annotation { "Feature Type Name" : "Feature", "Feature Type Description" : "" }
export const myFeature = defineFeature(function(context is Context, id is Id, definition is map)
    precondition{}
    {
        {
            var Q0;
            Q0=qCreatedBy(makeId("Top.planeOp"),FACE);
            var sketch = newSketch(context, id + "F0", { "sketchPlane" : qUnion([Q0])});
            skPoint(sketch, "E0.middle", {"position": v(0, 0) * mm});
            skLineSegment(sketch, "E1.bottom", {"start": v(-10, 19) * mm, "end": v(10, 19) * mm});
            skLineSegment(sketch, "E1.top", {"start": v(-10, -19) * mm, "end": v(10, -19) * mm});
            skLineSegment(sketch, "E1.left", {"start": v(-10, 19) * mm, "end": v(-10, -19) * mm});
            skLineSegment(sketch, "E1.right", {"start": v(10, 19) * mm, "end": v(10, -19) * mm});
            skArc(sketch, "E2.filletArc", {"start": v(-17, 30) * mm, "mid": v(-22.66, 27.66) * mm, "end": v(-25, 22) * mm});
            skPoint(sketch, "E3.visualSharp", {"position": v(25, 30) * mm});
            skArc(sketch, "E3.filletArc", {"start": v(25, 22) * mm, "mid": v(22.66, 27.66) * mm, "end": v(17, 30) * mm});
            skArc(sketch, "E4.filletArc", {"start": v(17, -30) * mm, "mid": v(22.66, -27.66) * mm, "end": v(25, -22) * mm});
            skArc(sketch, "E5.filletArc", {"start": v(-25, -22) * mm, "mid": v(-22.66, -27.66) * mm, "end": v(-17, -30) * mm});
            skCircle(sketch, "E6", {"center": v(-19, 24) * mm, "radius": 1.25 * mm});
            skCircle(sketch, "E7.MirrorC", {"center": v(19, 24) * mm, "radius": 1.25 * mm});
            skCircle(sketch, "E8.MirrorC", {"center": v(19, -24) * mm, "radius": 1.25 * mm});
            skCircle(sketch, "E9.MirrorC", {"center": v(-19, -24) * mm, "radius": 1.25 * mm});
            skLineSegment(sketch, "E10.bottom", {"start": v(-14.5, 18) * mm, "end": v(-12.5, 18) * mm});
            skLineSegment(sketch, "E10.top", {"start": v(-12.5, 6) * mm, "end": v(-12.5, 6) * mm});
            skLineSegment(sketch, "E10.left", {"start": v(-14.5, 18) * mm, "end": v(-14.5, 7.49) * mm});
            skLineSegment(sketch, "E10.right", {"start": v(-12.5, 18) * mm, "end": v(-12.5, 6) * mm});
            skLineSegment(sketch, "E11", {"start": v(-10, 25.5) * mm, "end": v(10, 25.5) * mm});
            skLineSegment(sketch, "E12", {"start": v(-17, 30) * mm, "end": v(-14, 30) * mm});
            skLineSegment(sketch, "E13", {"start": v(-10, 25.5) * mm, "end": v(-14, 30) * mm});
            skLineSegment(sketch, "E14", {"start": v(10, 25.5) * mm, "end": v(14, 30) * mm});
            skLineSegment(sketch, "E15", {"start": v(-17, -30) * mm, "end": v(-14, -30) * mm});
            skLineSegment(sketch, "E16", {"start": v(14, 30) * mm, "end": v(17, 30) * mm});
            skLineSegment(sketch, "E17", {"start": v(-14, -30) * mm, "end": v(-7.22, -22) * mm});
            skLineSegment(sketch, "E18", {"start": v(17, -30) * mm, "end": v(14, -30) * mm});
            skLineSegment(sketch, "E19", {"start": v(14, -30) * mm, "end": v(7.22, -22) * mm});
            skLineSegment(sketch, "E20", {"start": v(-25, -22) * mm, "end": v(-25, -19) * mm});
            skLineSegment(sketch, "E21", {"start": v(-25, 22) * mm, "end": v(-25, 19) * mm});
            skLineSegment(sketch, "E22", {"start": v(25, 22) * mm, "end": v(25, 19) * mm});
            skLineSegment(sketch, "E23", {"start": v(25, -22) * mm, "end": v(25, -19) * mm});
            skLineSegment(sketch, "E24", {"start": v(-20.5, -15) * mm, "end": v(-20.5, 15) * mm});
            skLineSegment(sketch, "E25", {"start": v(-25, -19) * mm, "end": v(-20.5, -15) * mm});
            skLineSegment(sketch, "E26", {"start": v(-20.5, 15) * mm, "end": v(-25, 19) * mm});
            skLineSegment(sketch, "E27", {"start": v(20.5, -15) * mm, "end": v(20.5, 15) * mm});
            skLineSegment(sketch, "E28", {"start": v(20.5, 15) * mm, "end": v(25, 19) * mm});
            skLineSegment(sketch, "E29", {"start": v(20.5, -15) * mm, "end": v(25, -19) * mm});
            skLineSegment(sketch, "E30", {"start": v(-9.92, -25.2) * mm, "end": v(-20.5, -15) * mm, "construction": true});
            skLineSegment(sketch, "E31", {"start": v(9.92, -25.2) * mm, "end": v(20.5, -15) * mm, "construction": true});
            skLineSegment(sketch, "E32", {"start": v(-20.5, 15) * mm, "end": v(-10, 25.5) * mm, "construction": true});
            skLineSegment(sketch, "E33", {"start": v(20.5, 15) * mm, "end": v(10, 25.5) * mm, "construction": true});
            skPoint(sketch, "E34.endSnap0", {"position": v(-20.5, 0) * mm});
            skArc(sketch, "E35.trimOffspring", {"start": v(-18.5, -6) * mm, "mid": v(-12.52, 0) * mm, "end": v(-18.5, 6) * mm});
            skArc(sketch, "E36.0", {"start": v(-18.5, -8.5) * mm, "mid": v(-10.02, 0) * mm, "end": v(-18.5, 8.5) * mm});
            skLineSegment(sketch, "E37", {"start": v(-18.5, 8.5) * mm, "end": v(-20.5, 8.5) * mm});
            skLineSegment(sketch, "E38", {"start": v(-18.5, 6) * mm, "end": v(-20.5, 6) * mm});
            skLineSegment(sketch, "E39", {"start": v(-18.5, -8.5) * mm, "end": v(-20.5, -8.5) * mm});
            skLineSegment(sketch, "E40", {"start": v(-18.5, -6) * mm, "end": v(-20.5, -6) * mm});
            skArc(sketch, "E41.MirrorCS", {"start": v(18.5, -8.5) * mm, "mid": v(10.02, 0) * mm, "end": v(18.5, 8.5) * mm});
            skArc(sketch, "E42.MirrorCS", {"start": v(18.5, -6) * mm, "mid": v(12.52, 0) * mm, "end": v(18.5, 6) * mm});
            skLineSegment(sketch, "E43.MirrorCS", {"start": v(18.5, -8.5) * mm, "end": v(20.5, -8.5) * mm});
            skLineSegment(sketch, "E44.MirrorCS", {"start": v(18.5, -6) * mm, "end": v(20.5, -6) * mm});
            skLineSegment(sketch, "E45.MirrorCS", {"start": v(18.5, 6) * mm, "end": v(20.5, 6) * mm});
            skLineSegment(sketch, "E46.MirrorCS", {"start": v(18.5, 8.5) * mm, "end": v(20.5, 8.5) * mm});
            skPoint(sketch, "E47.orphan", {"position": v(-14.5, 6) * mm});
            skLineSegment(sketch, "E48.MirrorCS", {"start": v(12.5, 18) * mm, "end": v(12.5, 6) * mm});
            skLineSegment(sketch, "E49.MirrorCS", {"start": v(14.5, 18) * mm, "end": v(14.5, 7.49) * mm});
            skLineSegment(sketch, "E50.MirrorCS", {"start": v(14.5, 18) * mm, "end": v(12.5, 18) * mm});
            skLineSegment(sketch, "E51.MirrorCS", {"start": v(14.5, -18) * mm, "end": v(14.5, -7.49) * mm});
            skLineSegment(sketch, "E52.MirrorCS", {"start": v(12.5, -18) * mm, "end": v(12.5, -6) * mm});
            skLineSegment(sketch, "E53.MirrorCS", {"start": v(14.5, -18) * mm, "end": v(12.5, -18) * mm});
            skLineSegment(sketch, "E54.MirrorCS", {"start": v(-12.5, -18) * mm, "end": v(-12.5, -6) * mm});
            skLineSegment(sketch, "E55.MirrorCS", {"start": v(-14.5, -18) * mm, "end": v(-14.5, -7.49) * mm});
            skLineSegment(sketch, "E56.MirrorCS", {"start": v(-14.5, -18) * mm, "end": v(-12.5, -18) * mm});
            skLineSegment(sketch, "E57.0", {"start": v(-7.22, -22) * mm, "end": v(7.22, -22) * mm});
            skLineSegment(sketch, "E58", {"start": v(0, 19) * mm, "end": v(0, 25.5) * mm, "construction": true});
            skLineSegment(sketch, "E59", {"start": v(-8.14, -19) * mm, "end": v(0, -2.79) * mm});
            skLineSegment(sketch, "E60", {"start": v(8.14, 19) * mm, "end": v(0, 2.79) * mm});
            skLineSegment(sketch, "E61", {"start": v(8.14, 19) * mm, "end": v(10, 19) * mm, "construction": true});
            skLineSegment(sketch, "E62", {"start": v(10, 17.14) * mm, "end": v(10, 19) * mm, "construction": true});
            skLineSegment(sketch, "E63", {"start": v(-8.14, -19) * mm, "end": v(-10, -19) * mm, "construction": true});
            skLineSegment(sketch, "E64", {"start": v(-10, -19) * mm, "end": v(-10, -17.14) * mm, "construction": true});
            skLineSegment(sketch, "E65.MirrorCS", {"start": v(-8.14, 19) * mm, "end": v(0, 2.79) * mm});
            skLineSegment(sketch, "E66.MirrorCS", {"start": v(8.14, -19) * mm, "end": v(0, -2.79) * mm});
            skLineSegment(sketch, "E67.trimOffspring", {"start": v(1.4, 0) * mm, "end": v(10, 17.14) * mm});
            skLineSegment(sketch, "E68.trimOffspring", {"start": v(-1.4, 0) * mm, "end": v(-10, -17.14) * mm});
            skLineSegment(sketch, "E69.trimOffspring", {"start": v(1.4, 0) * mm, "end": v(10, -17.14) * mm});
            skLineSegment(sketch, "E70.trimOffspring", {"start": v(-1.4, 0) * mm, "end": v(-10, 17.14) * mm});
            skSolve(sketch);
        }
        {
            var Q0;
            {var subQ23=sQuery(id+"F0.wireOp",EDGE,"E1.top");Q0=makeQuery(id+"F0.imprint","IMPRINT",FACE,{"disambiguationData":[TD([[makeQuery(id+"F0.imprint","IMPRINT",EDGE,{"derivedFrom":subQ23}),-1.0]])]});}
            var Q1;
            {var subQ18=sQuery(id+"F0.wireOp",EDGE,"E1.bottom");Q1=makeQuery(id+"F0.imprint","IMPRINT",FACE,{"disambiguationData":[TD([[makeQuery(id+"F0.imprint","IMPRINT",EDGE,{"derivedFrom":subQ18}),1.0]])]});}
            var Q2;
            {var subQ4=sQuery(id+"F0.wireOp",EDGE,"E10.top");Q2=makeQuery(id+"F0.imprint","IMPRINT",FACE,{"disambiguationData":[TD([[makeQuery(id+"F0.imprint","IMPRINT",EDGE,{"derivedFrom":subQ4}),-1.0]])]});}
            var Q3;
            Q3=makeQuery(id+"F0.imprint","IMPRINT",FACE,{"disambiguationData":[TD([[makeQuery(id+"F0.imprint","IMPRINT",EDGE,{"derivedFrom":sQuery(id+"F0.wireOp",EDGE,"E42.MirrorCS")}),1.0]])]});
            var Q4;
            Q4=makeQuery(id+"F0.imprint","IMPRINT",FACE,{"disambiguationData":[TD([[makeQuery(id+"F0.imprint","IMPRINT",EDGE,{"derivedFrom":sQuery(id+"F0.wireOp",EDGE,"E35.trimOffspring")}),-1.0]])]});
            var Q5;
            {var subQ13=sQuery(id+"F0.wireOp",EDGE,"E60");Q5=makeQuery(id+"F0.imprint","IMPRINT",FACE,{"disambiguationData":[TD([[makeQuery(id+"F0.imprint","IMPRINT",EDGE,{"derivedFrom":subQ13}),1.0]])]});}
            extrude(context, id + "F1", {"entities" : qUnion([Q0, Q1, Q2, Q3, Q4, Q5]), "depth" : 2 * mm});
        }
        {
            var Q0;
            Q0=makeQuery(id+"F1.opExtrude","CAP_FACE",FACE,{"disambiguationData":[OSD([sQuery(id+"F0.wireOp",EDGE,"E1.bottom"),sQuery(id+"F0.wireOp",EDGE,"E1.top"),sQuery(id+"F0.wireOp",EDGE,"E1.left"),sQuery(id+"F0.wireOp",EDGE,"E1.right"),sQuery(id+"F0.wireOp",EDGE,"E2.filletArc"),sQuery(id+"F0.wireOp",EDGE,"E3.filletArc"),sQuery(id+"F0.wireOp",EDGE,"E4.filletArc"),sQuery(id+"F0.wireOp",EDGE,"E5.filletArc"),sQuery(id+"F0.wireOp",EDGE,"E6"),sQuery(id+"F0.wireOp",EDGE,"E7.MirrorC"),sQuery(id+"F0.wireOp",EDGE,"E8.MirrorC"),sQuery(id+"F0.wireOp",EDGE,"E9.MirrorC"),sQuery(id+"F0.wireOp",EDGE,"E10.bottom"),sQuery(id+"F0.wireOp",EDGE,"E10.left"),sQuery(id+"F0.wireOp",EDGE,"E10.right"),sQuery(id+"F0.wireOp",EDGE,"E11"),sQuery(id+"F0.wireOp",EDGE,"E12"),sQuery(id+"F0.wireOp",EDGE,"E13"),sQuery(id+"F0.wireOp",EDGE,"E14"),sQuery(id+"F0.wireOp",EDGE,"E15"),sQuery(id+"F0.wireOp",EDGE,"E16"),sQuery(id+"F0.wireOp",EDGE,"E17"),sQuery(id+"F0.wireOp",EDGE,"E18"),sQuery(id+"F0.wireOp",EDGE,"E19"),sQuery(id+"F0.wireOp",EDGE,"E20"),sQuery(id+"F0.wireOp",EDGE,"E21"),sQuery(id+"F0.wireOp",EDGE,"E22"),sQuery(id+"F0.wireOp",EDGE,"E23"),sQuery(id+"F0.wireOp",EDGE,"E24"),sQuery(id+"F0.wireOp",EDGE,"E25"),sQuery(id+"F0.wireOp",EDGE,"E26"),sQuery(id+"F0.wireOp",EDGE,"E27"),sQuery(id+"F0.wireOp",EDGE,"E28"),sQuery(id+"F0.wireOp",EDGE,"E29"),sQuery(id+"F0.wireOp",EDGE,"E35.trimOffspring"),sQuery(id+"F0.wireOp",EDGE,"E36.0"),sQuery(id+"F0.wireOp",EDGE,"E38"),sQuery(id+"F0.wireOp",EDGE,"E40"),sQuery(id+"F0.wireOp",EDGE,"E41.MirrorCS"),sQuery(id+"F0.wireOp",EDGE,"E42.MirrorCS"),sQuery(id+"F0.wireOp",EDGE,"E44.MirrorCS"),sQuery(id+"F0.wireOp",EDGE,"E45.MirrorCS"),sQuery(id+"F0.wireOp",EDGE,"E48.MirrorCS"),sQuery(id+"F0.wireOp",EDGE,"E49.MirrorCS"),sQuery(id+"F0.wireOp",EDGE,"E50.MirrorCS"),sQuery(id+"F0.wireOp",EDGE,"E51.MirrorCS"),sQuery(id+"F0.wireOp",EDGE,"E52.MirrorCS"),sQuery(id+"F0.wireOp",EDGE,"E53.MirrorCS"),sQuery(id+"F0.wireOp",EDGE,"E54.MirrorCS"),sQuery(id+"F0.wireOp",EDGE,"E55.MirrorCS"),sQuery(id+"F0.wireOp",EDGE,"E56.MirrorCS"),sQuery(id+"F0.wireOp",EDGE,"KbkjGo9e-Lsoh-N3L6-NFuE-XmgJdDSsoZK0")])],"isStart":false});
            var Q1;
            Q1=makeQuery(id+"F1.opExtrude","CAP_FACE",FACE,{"disambiguationData":[OSD([sQuery(id+"F0.wireOp",EDGE,"E1.bottom"),sQuery(id+"F0.wireOp",EDGE,"E1.top"),sQuery(id+"F0.wireOp",EDGE,"E1.left"),sQuery(id+"F0.wireOp",EDGE,"E1.right"),sQuery(id+"F0.wireOp",EDGE,"E2.filletArc"),sQuery(id+"F0.wireOp",EDGE,"E3.filletArc"),sQuery(id+"F0.wireOp",EDGE,"E4.filletArc"),sQuery(id+"F0.wireOp",EDGE,"E5.filletArc"),sQuery(id+"F0.wireOp",EDGE,"E6"),sQuery(id+"F0.wireOp",EDGE,"E7.MirrorC"),sQuery(id+"F0.wireOp",EDGE,"E8.MirrorC"),sQuery(id+"F0.wireOp",EDGE,"E9.MirrorC"),sQuery(id+"F0.wireOp",EDGE,"E10.bottom"),sQuery(id+"F0.wireOp",EDGE,"E10.left"),sQuery(id+"F0.wireOp",EDGE,"E10.right"),sQuery(id+"F0.wireOp",EDGE,"E11"),sQuery(id+"F0.wireOp",EDGE,"E12"),sQuery(id+"F0.wireOp",EDGE,"E13"),sQuery(id+"F0.wireOp",EDGE,"E14"),sQuery(id+"F0.wireOp",EDGE,"E15"),sQuery(id+"F0.wireOp",EDGE,"E16"),sQuery(id+"F0.wireOp",EDGE,"E17"),sQuery(id+"F0.wireOp",EDGE,"E18"),sQuery(id+"F0.wireOp",EDGE,"E19"),sQuery(id+"F0.wireOp",EDGE,"E20"),sQuery(id+"F0.wireOp",EDGE,"E21"),sQuery(id+"F0.wireOp",EDGE,"E22"),sQuery(id+"F0.wireOp",EDGE,"E23"),sQuery(id+"F0.wireOp",EDGE,"E24"),sQuery(id+"F0.wireOp",EDGE,"E25"),sQuery(id+"F0.wireOp",EDGE,"E26"),sQuery(id+"F0.wireOp",EDGE,"E27"),sQuery(id+"F0.wireOp",EDGE,"E28"),sQuery(id+"F0.wireOp",EDGE,"E29"),sQuery(id+"F0.wireOp",EDGE,"E35.trimOffspring"),sQuery(id+"F0.wireOp",EDGE,"E36.0"),sQuery(id+"F0.wireOp",EDGE,"E38"),sQuery(id+"F0.wireOp",EDGE,"E40"),sQuery(id+"F0.wireOp",EDGE,"E41.MirrorCS"),sQuery(id+"F0.wireOp",EDGE,"E42.MirrorCS"),sQuery(id+"F0.wireOp",EDGE,"E44.MirrorCS"),sQuery(id+"F0.wireOp",EDGE,"E45.MirrorCS"),sQuery(id+"F0.wireOp",EDGE,"E48.MirrorCS"),sQuery(id+"F0.wireOp",EDGE,"E49.MirrorCS"),sQuery(id+"F0.wireOp",EDGE,"E50.MirrorCS"),sQuery(id+"F0.wireOp",EDGE,"E51.MirrorCS"),sQuery(id+"F0.wireOp",EDGE,"E52.MirrorCS"),sQuery(id+"F0.wireOp",EDGE,"E53.MirrorCS"),sQuery(id+"F0.wireOp",EDGE,"E54.MirrorCS"),sQuery(id+"F0.wireOp",EDGE,"E55.MirrorCS"),sQuery(id+"F0.wireOp",EDGE,"E56.MirrorCS"),sQuery(id+"F0.wireOp",EDGE,"KbkjGo9e-Lsoh-N3L6-NFuE-XmgJdDSsoZK0")])],"isStart":true});
            var Q2;
            Q2=makeQuery(id+"F1.opExtrude","SWEPT_EDGE",EDGE,{"disambiguationData":[OSD([sQuery(id+"F0.wireOp",EDGE,"E24"),sQuery(id+"F0.wireOp",EDGE,"E38")])]});
            var Q3;
            Q3=makeQuery(id+"F1.opExtrude","SWEPT_EDGE",EDGE,{"disambiguationData":[OSD([sQuery(id+"F0.wireOp",EDGE,"E24"),sQuery(id+"F0.wireOp",EDGE,"E40")])]});
            var Q4;
            Q4=makeQuery(id+"F1.opExtrude","SWEPT_EDGE",EDGE,{"disambiguationData":[OSD([sQuery(id+"F0.wireOp",EDGE,"E27"),sQuery(id+"F0.wireOp",EDGE,"E44.MirrorCS")])]});
            var Q5;
            Q5=makeQuery(id+"F1.opExtrude","SWEPT_EDGE",EDGE,{"disambiguationData":[OSD([sQuery(id+"F0.wireOp",EDGE,"E27"),sQuery(id+"F0.wireOp",EDGE,"E45.MirrorCS")])]});
            fillet(context, id + "F2", {"entities" : qUnion([Q0, Q1, Q2, Q3, Q4, Q5]), "radius" : .5 * mm, "tangentPropagation" : true, "allowEdgeOverflow" : false});
        }
    });